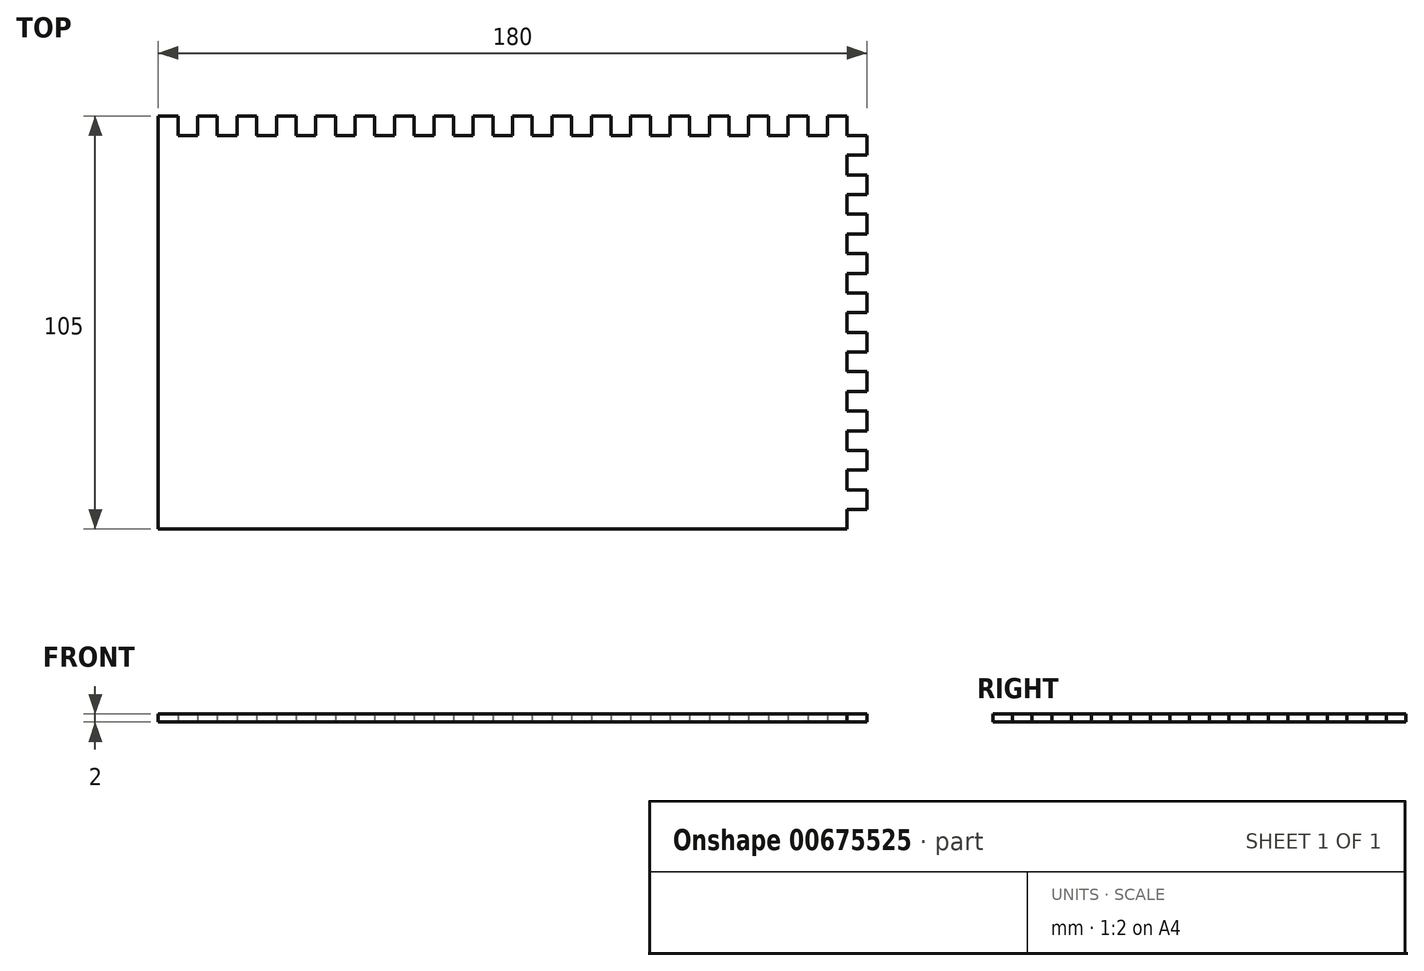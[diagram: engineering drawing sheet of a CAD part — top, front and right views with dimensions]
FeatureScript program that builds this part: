
annotation { "Feature Type Name" : "Feature", "Feature Type Description" : "" }
export const myFeature = defineFeature(function(context is Context, id is Id, definition is map)
    precondition{}
    {
        {
            var Q0;
            Q0=qCreatedBy(makeId("Top.planeOp"),FACE);
            var sketch = newSketch(context, id + "F0", { "sketchPlane" : qUnion([Q0])});
            skLineSegment(sketch, "E0", {"start": v(-180, -103.5) * mm, "end": v(-5, -103.5) * mm});
            skLineSegment(sketch, "E1", {"start": v(0, -3.5) * mm, "end": v(0, -8.5) * mm});
            skLineSegment(sketch, "E2", {"start": v(-180, 1.5) * mm, "end": v(-180, -3.5) * mm});
            skLineSegment(sketch, "E3", {"start": v(-180, 1.5) * mm, "end": v(-175, 1.5) * mm});
            skLineSegment(sketch, "E4", {"start": v(-170, 1.5) * mm, "end": v(-165, 1.5) * mm});
            skLineSegment(sketch, "E5", {"start": v(-160, 1.5) * mm, "end": v(-155, 1.5) * mm});
            skLineSegment(sketch, "E6", {"start": v(-150, 1.5) * mm, "end": v(-145, 1.5) * mm});
            skLineSegment(sketch, "E7", {"start": v(-140, 1.5) * mm, "end": v(-135, 1.5) * mm});
            skLineSegment(sketch, "E8", {"start": v(-130, 1.5) * mm, "end": v(-125, 1.5) * mm});
            skLineSegment(sketch, "E9", {"start": v(-120, 1.5) * mm, "end": v(-115, 1.5) * mm});
            skLineSegment(sketch, "E10", {"start": v(-110, 1.5) * mm, "end": v(-105, 1.5) * mm});
            skLineSegment(sketch, "E11", {"start": v(-100, 1.5) * mm, "end": v(-95, 1.5) * mm});
            skLineSegment(sketch, "E12", {"start": v(-90, 1.5) * mm, "end": v(-85, 1.5) * mm});
            skLineSegment(sketch, "E13", {"start": v(-80, 1.5) * mm, "end": v(-75, 1.5) * mm});
            skLineSegment(sketch, "E14", {"start": v(-70, 1.5) * mm, "end": v(-65, 1.5) * mm});
            skLineSegment(sketch, "E15", {"start": v(-60, 1.5) * mm, "end": v(-55, 1.5) * mm});
            skLineSegment(sketch, "E16", {"start": v(-50, 1.5) * mm, "end": v(-45, 1.5) * mm});
            skLineSegment(sketch, "E17", {"start": v(-40, 1.5) * mm, "end": v(-35, 1.5) * mm});
            skLineSegment(sketch, "E18", {"start": v(-30, 1.5) * mm, "end": v(-25, 1.5) * mm});
            skLineSegment(sketch, "E19", {"start": v(-20, 1.5) * mm, "end": v(-15, 1.5) * mm});
            skLineSegment(sketch, "E20", {"start": v(-10, 1.5) * mm, "end": v(-5, 1.5) * mm});
            skLineSegment(sketch, "E21", {"start": v(-180, -3.5) * mm, "end": v(-180, -103.5) * mm});
            skLineSegment(sketch, "E22", {"start": v(-175, -3.5) * mm, "end": v(-170, -3.5) * mm});
            skLineSegment(sketch, "E23", {"start": v(-175, 1.5) * mm, "end": v(-175, -3.5) * mm});
            skLineSegment(sketch, "E24", {"start": v(-170, 1.5) * mm, "end": v(-170, -3.5) * mm});
            skLineSegment(sketch, "E25", {"start": v(-165, 1.5) * mm, "end": v(-165, -3.5) * mm});
            skLineSegment(sketch, "E26", {"start": v(-160, 1.5) * mm, "end": v(-160, -3.5) * mm});
            skLineSegment(sketch, "E27", {"start": v(-155, 1.5) * mm, "end": v(-155, -3.5) * mm});
            skLineSegment(sketch, "E28", {"start": v(-150, 1.5) * mm, "end": v(-150, -3.5) * mm});
            skLineSegment(sketch, "E29", {"start": v(-145, 1.5) * mm, "end": v(-145, -3.5) * mm});
            skLineSegment(sketch, "E30", {"start": v(-140, 1.5) * mm, "end": v(-140, -3.5) * mm});
            skLineSegment(sketch, "E31", {"start": v(-135, 1.5) * mm, "end": v(-135, -3.5) * mm});
            skLineSegment(sketch, "E32", {"start": v(-130, 1.5) * mm, "end": v(-130, -3.5) * mm});
            skLineSegment(sketch, "E33", {"start": v(-125, 1.5) * mm, "end": v(-125, -3.5) * mm});
            skLineSegment(sketch, "E34", {"start": v(-85, 1.5) * mm, "end": v(-85, -3.5) * mm});
            skLineSegment(sketch, "E35", {"start": v(-80, 1.5) * mm, "end": v(-80, -3.5) * mm});
            skLineSegment(sketch, "E36", {"start": v(-75, 1.5) * mm, "end": v(-75, -3.5) * mm});
            skLineSegment(sketch, "E37", {"start": v(-70, 1.5) * mm, "end": v(-70, -3.5) * mm});
            skLineSegment(sketch, "E38", {"start": v(-65, 1.5) * mm, "end": v(-65, -3.5) * mm});
            skLineSegment(sketch, "E39", {"start": v(-60, 1.5) * mm, "end": v(-60, -3.5) * mm});
            skLineSegment(sketch, "E40", {"start": v(-55, 1.5) * mm, "end": v(-55, -3.5) * mm});
            skLineSegment(sketch, "E41", {"start": v(-50, 1.5) * mm, "end": v(-50, -3.5) * mm});
            skLineSegment(sketch, "E42", {"start": v(-45, 1.5) * mm, "end": v(-45, -3.5) * mm});
            skLineSegment(sketch, "E43", {"start": v(-40, 1.5) * mm, "end": v(-40, -3.5) * mm});
            skLineSegment(sketch, "E44", {"start": v(-35, 1.5) * mm, "end": v(-35, -3.5) * mm});
            skLineSegment(sketch, "E45", {"start": v(-30, 1.5) * mm, "end": v(-30, -3.5) * mm});
            skLineSegment(sketch, "E46", {"start": v(-25, 1.5) * mm, "end": v(-25, -3.5) * mm});
            skLineSegment(sketch, "E47", {"start": v(-20, 1.5) * mm, "end": v(-20, -3.5) * mm});
            skLineSegment(sketch, "E48", {"start": v(-15, 1.5) * mm, "end": v(-15, -3.5) * mm});
            skLineSegment(sketch, "E49", {"start": v(-10, 1.5) * mm, "end": v(-10, -3.5) * mm});
            skLineSegment(sketch, "E50", {"start": v(-5, 1.5) * mm, "end": v(-5, -3.5) * mm});
            skLineSegment(sketch, "E51.MirrorCS", {"start": v(-180, 1.5) * mm, "end": v(-175, 1.5) * mm, "construction": true});
            skLineSegment(sketch, "E52.trimOffspring", {"start": v(-165, -3.5) * mm, "end": v(-160, -3.5) * mm});
            skLineSegment(sketch, "E53.trimOffspring", {"start": v(-155, -3.5) * mm, "end": v(-150, -3.5) * mm});
            skLineSegment(sketch, "E54.trimOffspring", {"start": v(-145, -3.5) * mm, "end": v(-140, -3.5) * mm});
            skLineSegment(sketch, "E55.trimOffspring", {"start": v(-135, -3.5) * mm, "end": v(-130, -3.5) * mm});
            skLineSegment(sketch, "E56.trimOffspring", {"start": v(-125, -3.5) * mm, "end": v(-120, -3.5) * mm});
            skLineSegment(sketch, "E57.trimOffspring", {"start": v(-115, -3.5) * mm, "end": v(-110, -3.5) * mm});
            skLineSegment(sketch, "E58.trimOffspring", {"start": v(-105, -3.5) * mm, "end": v(-100, -3.5) * mm});
            skLineSegment(sketch, "E59.trimOffspring", {"start": v(-95, -3.5) * mm, "end": v(-90, -3.5) * mm});
            skLineSegment(sketch, "E60.trimOffspring", {"start": v(-85, -3.5) * mm, "end": v(-80, -3.5) * mm});
            skLineSegment(sketch, "E61.trimOffspring", {"start": v(-75, -3.5) * mm, "end": v(-70, -3.5) * mm});
            skLineSegment(sketch, "E62.trimOffspring", {"start": v(-65, -3.5) * mm, "end": v(-60, -3.5) * mm});
            skLineSegment(sketch, "E63.trimOffspring", {"start": v(-55, -3.5) * mm, "end": v(-50, -3.5) * mm});
            skLineSegment(sketch, "E64.trimOffspring", {"start": v(-45, -3.5) * mm, "end": v(-40, -3.5) * mm});
            skLineSegment(sketch, "E65.trimOffspring", {"start": v(-25, -3.5) * mm, "end": v(-20, -3.5) * mm});
            skLineSegment(sketch, "E66.trimOffspring", {"start": v(-5, -3.5) * mm, "end": v(0, -3.5) * mm});
            skLineSegment(sketch, "E67.trimOffspring", {"start": v(-15, -3.5) * mm, "end": v(-10, -3.5) * mm});
            skLineSegment(sketch, "E68", {"start": v(-30, -3.5) * mm, "end": v(-35, -3.5) * mm});
            skLineSegment(sketch, "E69", {"start": v(-5, -3.5) * mm, "end": v(-5, -103.5) * mm});
            skLineSegment(sketch, "E70", {"start": v(-5, -8.5) * mm, "end": v(0, -8.5) * mm});
            skLineSegment(sketch, "E71", {"start": v(-5, -13.5) * mm, "end": v(0, -13.5) * mm});
            skLineSegment(sketch, "E72", {"start": v(-5, -18.5) * mm, "end": v(0, -18.5) * mm});
            skLineSegment(sketch, "E73", {"start": v(0, -23.5) * mm, "end": v(-5, -23.5) * mm});
            skLineSegment(sketch, "E74", {"start": v(-5, -28.5) * mm, "end": v(0, -28.5) * mm});
            skLineSegment(sketch, "E75", {"start": v(-5, -33.5) * mm, "end": v(0, -33.5) * mm});
            skLineSegment(sketch, "E76", {"start": v(0, -38.5) * mm, "end": v(-5, -38.5) * mm});
            skLineSegment(sketch, "E77", {"start": v(-5, -43.5) * mm, "end": v(0, -43.5) * mm});
            skLineSegment(sketch, "E78", {"start": v(0, -48.5) * mm, "end": v(-5, -48.5) * mm});
            skLineSegment(sketch, "E79", {"start": v(-5, -53.5) * mm, "end": v(0, -53.5) * mm});
            skLineSegment(sketch, "E80", {"start": v(0, -58.5) * mm, "end": v(-5, -58.5) * mm});
            skLineSegment(sketch, "E81", {"start": v(-5, -63.5) * mm, "end": v(0, -63.5) * mm});
            skLineSegment(sketch, "E82", {"start": v(-5, -68.5) * mm, "end": v(0, -68.5) * mm});
            skLineSegment(sketch, "E83", {"start": v(-5, -73.5) * mm, "end": v(0, -73.5) * mm});
            skLineSegment(sketch, "E84", {"start": v(-5, -78.5) * mm, "end": v(0, -78.5) * mm});
            skLineSegment(sketch, "E85", {"start": v(-5, -83.5) * mm, "end": v(0, -83.5) * mm});
            skLineSegment(sketch, "E86", {"start": v(-5, -88.5) * mm, "end": v(0, -88.5) * mm});
            skLineSegment(sketch, "E87", {"start": v(-5, -93.5) * mm, "end": v(0, -93.5) * mm});
            skLineSegment(sketch, "E88", {"start": v(-5, -98.5) * mm, "end": v(0, -98.5) * mm});
            skLineSegment(sketch, "E89.trimOffspring", {"start": v(0, -13.5) * mm, "end": v(0, -18.5) * mm});
            skLineSegment(sketch, "E90.trimOffspring", {"start": v(0, -23.5) * mm, "end": v(0, -28.5) * mm});
            skLineSegment(sketch, "E91.trimOffspring", {"start": v(0, -33.5) * mm, "end": v(0, -38.5) * mm});
            skLineSegment(sketch, "E92.trimOffspring", {"start": v(0, -43.5) * mm, "end": v(0, -48.5) * mm});
            skLineSegment(sketch, "E93.trimOffspring", {"start": v(0, -53.5) * mm, "end": v(0, -58.5) * mm});
            skLineSegment(sketch, "E94.trimOffspring", {"start": v(0, -63.5) * mm, "end": v(0, -68.5) * mm});
            skLineSegment(sketch, "E95.trimOffspring", {"start": v(0, -83.5) * mm, "end": v(0, -88.5) * mm});
            skLineSegment(sketch, "E96", {"start": v(-120, -3.5) * mm, "end": v(-120, 1.5) * mm});
            skLineSegment(sketch, "E97", {"start": v(-115, 1.5) * mm, "end": v(-115, -3.5) * mm});
            skLineSegment(sketch, "E98", {"start": v(-110, -3.5) * mm, "end": v(-110, 1.5) * mm});
            skLineSegment(sketch, "E99", {"start": v(-105, 1.5) * mm, "end": v(-105, -3.5) * mm});
            skLineSegment(sketch, "E100", {"start": v(-100, 1.5) * mm, "end": v(-100, -3.5) * mm});
            skLineSegment(sketch, "E101", {"start": v(-95, 1.5) * mm, "end": v(-95, -3.5) * mm});
            skLineSegment(sketch, "E102", {"start": v(-90, 1.5) * mm, "end": v(-90, -3.5) * mm});
            skLineSegment(sketch, "E103", {"start": v(0, -78.5) * mm, "end": v(0, -73.5) * mm});
            skLineSegment(sketch, "E104.trimOffspring", {"start": v(0, -93.5) * mm, "end": v(0, -98.5) * mm});
            skSolve(sketch);
        }
        {
            var Q0;
            Q0 = qSketchRegion(id + "F0", true);
            extrude(context, id + "F1", {"entities" : qUnion([Q0]), "depth" : 2 * mm, "offsetDistance" : 25 * mm});
        }
    });
